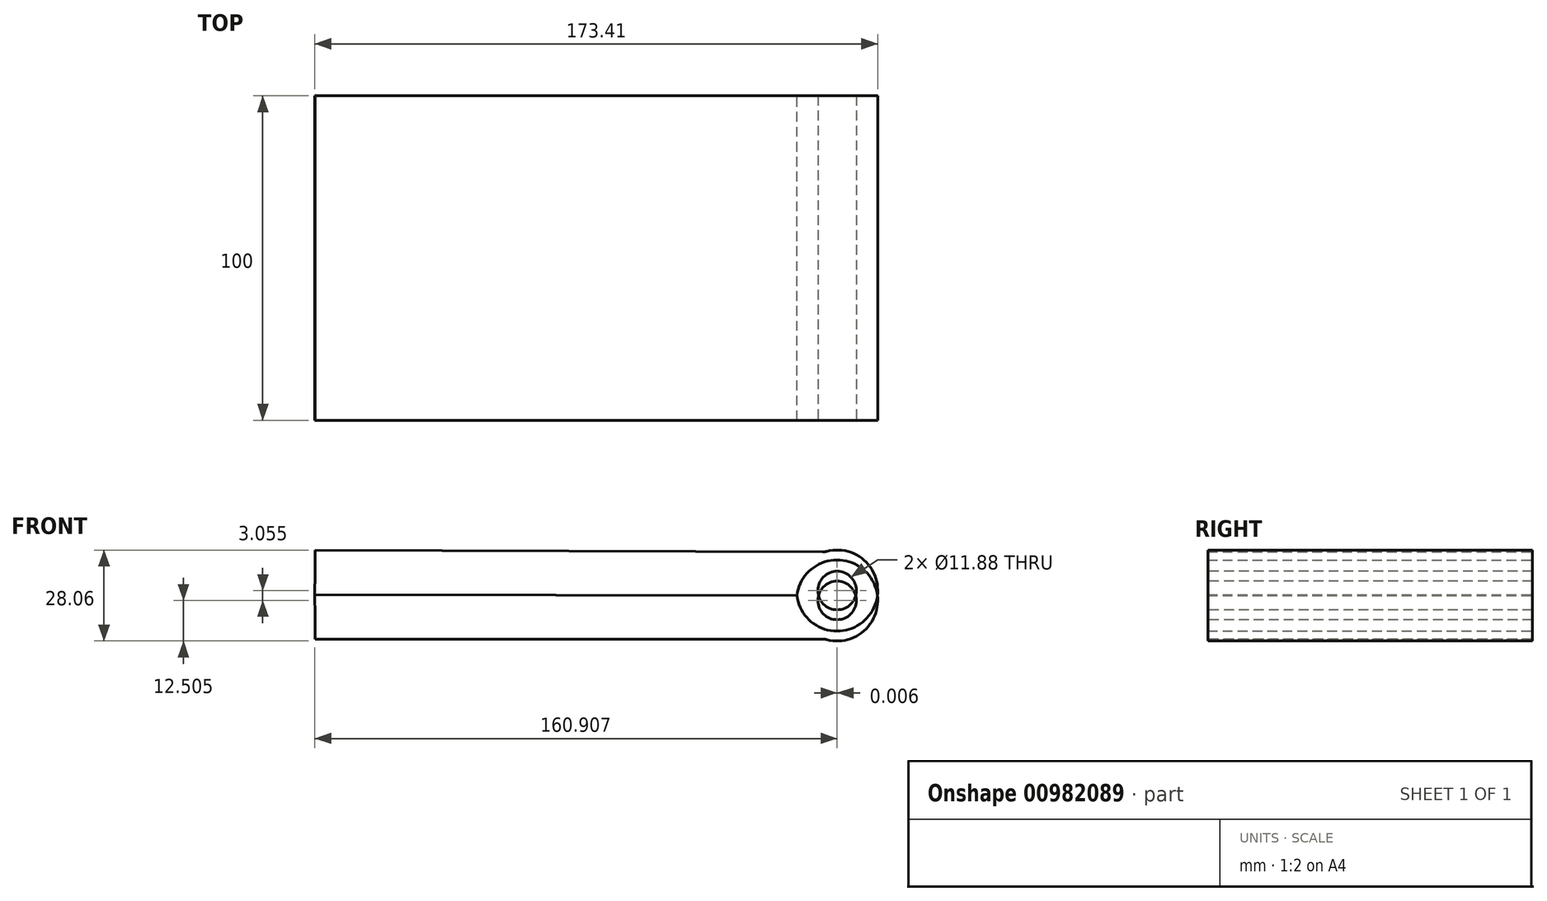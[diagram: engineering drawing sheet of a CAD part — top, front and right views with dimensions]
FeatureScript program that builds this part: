
annotation { "Feature Type Name" : "Feature", "Feature Type Description" : "" }
export const myFeature = defineFeature(function(context is Context, id is Id, definition is map)
    precondition{}
    {
        {
            var Q0;
            Q0=qCreatedBy(makeId("Front.planeOp"),FACE);
            var sketch = newSketch(context, id + "F0", { "sketchPlane" : qUnion([Q0])});
            skLineSegment(sketch, "E0", {"start": v(36.18, -6.73) * mm, "end": v(-114.14, -6.73) * mm});
            skLineSegment(sketch, "E1", {"start": v(-114.14, -6.73) * mm, "end": v(-114.14, 0.27) * mm});
            skArc(sketch, "E2", {"start": v(42.88, -6.73) * mm, "mid": v(57.29, 11.87) * mm, "end": v(34.33, 6.72) * mm});
            skArc(sketch, "E3", {"start": v(42.31, 2.83) * mm, "mid": v(51.19, 7.45) * mm, "end": v(42.26, 2.93) * mm});
            skLineSegment(sketch, "E4", {"start": v(36.18, -6.73) * mm, "end": v(42.88, -6.73) * mm});
            skLineSegment(sketch, "E5", {"start": v(-114.17, 7) * mm, "end": v(-114.14, 0.27) * mm});
            skPoint(sketch, "E6.end.orphan", {"position": v(-118.3, 0) * mm});
            skLineSegment(sketch, "E7", {"start": v(34.33, 6.72) * mm, "end": v(-114.17, 7) * mm});
            skSolve(sketch);
        }
        {
            var Q0;
            Q0=makeQuery(id+"F0.imprint","IMPRINT",FACE,{"disambiguationData":[TD([[makeQuery(id+"F0.imprint","IMPRINT",EDGE,{"derivedFrom":sQuery(id+"F0.wireOp",EDGE,"E0")}),-1.0]])]});
            extrude(context, id + "F1", {"entities" : qUnion([Q0]), "depth" : 100 * mm, "offsetDistance" : 25 * mm});
        }
        {
            var Q0;
            Q0=makeQuery(id+"F1.opExtrude","SWEPT_EDGE",EDGE,{"disambiguationData":[OSD([sQuery(id+"F0.wireOp",EDGE,"E2"),sQuery(id+"F0.wireOp",EDGE,"E4")])]});
            fillet(context, id + "F2", {"entities" : qUnion([Q0]), "radius" : 5 * mm, "tangentPropagation" : true, "rho" : 0.5, "crossSection" : FilletCrossSection.CONIC, "allowEdgeOverflow" : false});
        }
        {
            var Q0;
            Q0=makeQuery(id+"F1.opExtrude","CAP_FACE",FACE,{"disambiguationData":[OSD([sQuery(id+"F0.wireOp",EDGE,"E0"),sQuery(id+"F0.wireOp",EDGE,"E1"),sQuery(id+"F0.wireOp",EDGE,"E6"),sQuery(id+"F0.wireOp",EDGE,"E2"),sQuery(id+"F0.wireOp",EDGE,"2c31d08a-dca7-4a21-8633-4873f0852020"),sQuery(id+"F0.wireOp",EDGE,"E4")])],"isStart":false});
            var sketch = newSketch(context, id + "F3", { "sketchPlane" : qUnion([Q0])});
            skCircle(sketch, "E8", {"center": v(46.74, 5.16) * mm, "radius": 5.94 * mm});
            skSolve(sketch);
        }
        {
            var Q0;
            Q0=makeQuery(id+"F3.imprint","IMPRINT",FACE,{"disambiguationData":[TD([[makeQuery(id+"F3.imprint","IMPRINT",EDGE,{"derivedFrom":sQuery(id+"F3.wireOp",EDGE,"E8")}),1.0]])]});
            extrude(context, id + "F4", {"entities" : qUnion([Q0]), "operationType" : NewBodyOperationType.REMOVE, "oppositeDirection" : true, "depth" : 167.9 * mm, "offsetDistance" : 25 * mm});
        }
        {
            var Q0;
            Q0=makeQuery(id+"F1.opExtrude","SWEPT_BODY",BODY,{"disambiguationData":[OSD([sQuery(id+"F0.wireOp",EDGE,"E0"),sQuery(id+"F0.wireOp",EDGE,"E1"),sQuery(id+"F0.wireOp",EDGE,"E2"),sQuery(id+"F0.wireOp",EDGE,"E4"),sQuery(id+"F0.wireOp",EDGE,"E5"),sQuery(id+"F0.wireOp",EDGE,"E7")])]});
            var Q1;
            Q1=makeQuery(id+"F1.opExtrude","SWEPT_FACE",FACE,{"disambiguationData":[OSD([sQuery(id+"F0.wireOp",EDGE,"E7")])]});
            mirror(context, id + "F5", {"entities" : qUnion([Q0]), "mirrorPlane" : qUnion([Q1])});
        }
    });
